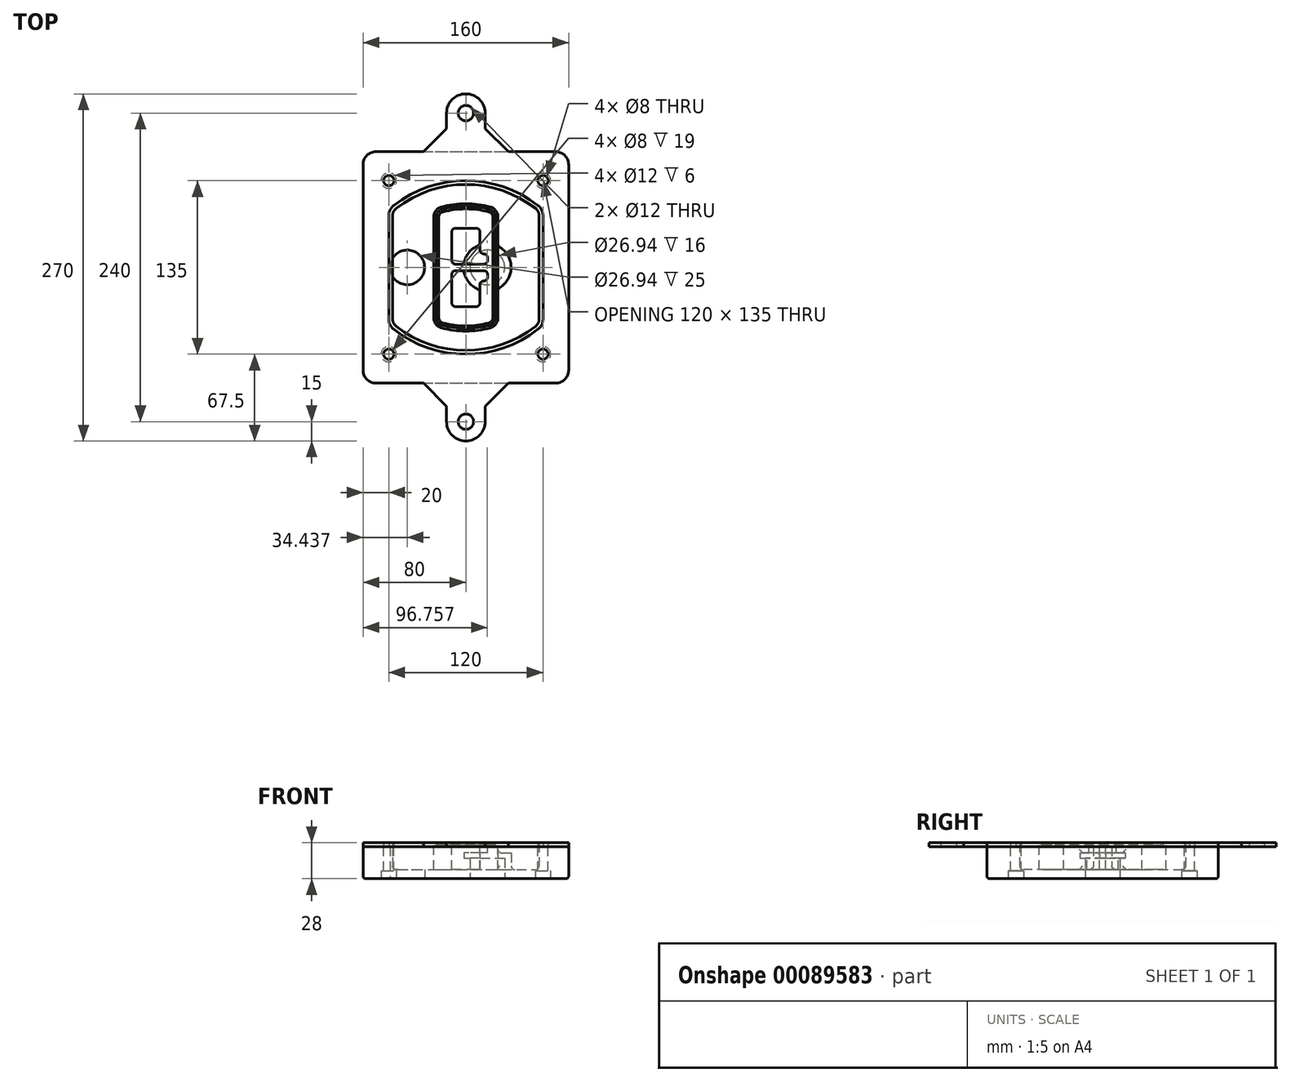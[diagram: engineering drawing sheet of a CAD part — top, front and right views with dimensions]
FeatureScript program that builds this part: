
annotation { "Feature Type Name" : "Feature", "Feature Type Description" : "" }
export const myFeature = defineFeature(function(context is Context, id is Id, definition is map)
    precondition{}
    {
        {
            var Q0;
            Q0=qCreatedBy(makeId("Top.planeOp"),FACE);
            var sketch = newSketch(context, id + "F0", { "sketchPlane" : qUnion([Q0])});
            skPoint(sketch, "E0.rect.middle", {"position": v(0, 0) * mm});
            skLineSegment(sketch, "E1.bottom", {"start": v(-70, -90) * mm, "end": v(70, -90) * mm});
            skLineSegment(sketch, "E1.top", {"start": v(-70, 90) * mm, "end": v(70, 90) * mm});
            skLineSegment(sketch, "E1.left", {"start": v(-80, -80) * mm, "end": v(-80, 80) * mm});
            skLineSegment(sketch, "E1.right", {"start": v(80, -80) * mm, "end": v(80, 80) * mm});
            skLineSegment(sketch, "E2", {"start": v(-80, 90) * mm, "end": v(80, -90) * mm, "construction": true});
            skLineSegment(sketch, "E3", {"start": v(80, 90) * mm, "end": v(-80, -90) * mm, "construction": true});
            skCircle(sketch, "E4", {"center": v(-60, 67.5) * mm, "radius": 4 * mm});
            skCircle(sketch, "E5", {"center": v(60, 67.5) * mm, "radius": 4 * mm});
            skCircle(sketch, "E6", {"center": v(60, -67.5) * mm, "radius": 4 * mm});
            skCircle(sketch, "E7", {"center": v(-60, -67.5) * mm, "radius": 4 * mm});
            skLineSegment(sketch, "E8", {"start": v(-60, 67.5) * mm, "end": v(60, 67.5) * mm, "construction": true});
            skLineSegment(sketch, "E9", {"start": v(60, 67.5) * mm, "end": v(60, -67.5) * mm, "construction": true});
            skLineSegment(sketch, "E10", {"start": v(60, -67.5) * mm, "end": v(-60, -67.5) * mm, "construction": true});
            skLineSegment(sketch, "E11", {"start": v(-60, -67.5) * mm, "end": v(-60, 67.5) * mm, "construction": true});
            skLineSegment(sketch, "E12", {"start": v(-60, 40.3) * mm, "end": v(-60, -40.3) * mm});
            skLineSegment(sketch, "E13", {"start": v(60, 40.3) * mm, "end": v(60, -40.3) * mm});
            skArc(sketch, "E14", {"start": v(56.15, 48.18) * mm, "mid": v(0, 67.5) * mm, "end": v(-56.15, 48.18) * mm});
            skArc(sketch, "E15", {"start": v(-56.15, -48.18) * mm, "mid": v(0, -67.5) * mm, "end": v(56.15, -48.18) * mm});
            skLineSegment(sketch, "E16", {"start": v(-60, 0) * mm, "end": v(60, 0) * mm, "construction": true});
            skPoint(sketch, "E17.visualSharp", {"position": v(-60, -45) * mm});
            skArc(sketch, "E17.filletArc", {"start": v(-60, -40.3) * mm, "mid": v(-58.99, -44.68) * mm, "end": v(-56.15, -48.18) * mm});
            skPoint(sketch, "E18.visualSharp", {"position": v(-60, 45) * mm});
            skArc(sketch, "E18.filletArc", {"start": v(-56.15, 48.18) * mm, "mid": v(-58.99, 44.68) * mm, "end": v(-60, 40.3) * mm});
            skPoint(sketch, "E19.visualSharp", {"position": v(60, 45) * mm});
            skArc(sketch, "E19.filletArc", {"start": v(60, 40.3) * mm, "mid": v(58.99, 44.68) * mm, "end": v(56.15, 48.18) * mm});
            skPoint(sketch, "E20.visualSharp", {"position": v(60, -45) * mm});
            skArc(sketch, "E20.filletArc", {"start": v(56.15, -48.18) * mm, "mid": v(58.99, -44.68) * mm, "end": v(60, -40.3) * mm});
            skPoint(sketch, "E21.visualSharp", {"position": v(-80, 90) * mm});
            skArc(sketch, "E21.filletArc", {"start": v(-70, 90) * mm, "mid": v(-77.07, 87.07) * mm, "end": v(-80, 80) * mm});
            skPoint(sketch, "E22.visualSharp", {"position": v(80, 90) * mm});
            skArc(sketch, "E22.filletArc", {"start": v(80, 80) * mm, "mid": v(77.07, 87.07) * mm, "end": v(70, 90) * mm});
            skPoint(sketch, "E23.visualSharp", {"position": v(80, -90) * mm});
            skArc(sketch, "E23.filletArc", {"start": v(70, -90) * mm, "mid": v(77.07, -87.07) * mm, "end": v(80, -80) * mm});
            skPoint(sketch, "E24.visualSharp", {"position": v(-80, -90) * mm});
            skArc(sketch, "E24.filletArc", {"start": v(-80, -80) * mm, "mid": v(-77.07, -87.07) * mm, "end": v(-70, -90) * mm});
            skArc(sketch, "E25.0", {"start": v(57, 40.3) * mm, "mid": v(56.3, 43.36) * mm, "end": v(54.3, 45.81) * mm});
            skLineSegment(sketch, "E25.1", {"start": v(57, 40.3) * mm, "end": v(57, -40.3) * mm});
            skArc(sketch, "E25.2", {"start": v(54.3, -45.81) * mm, "mid": v(56.3, -43.36) * mm, "end": v(57, -40.3) * mm});
            skArc(sketch, "E25.3", {"start": v(-54.3, -45.81) * mm, "mid": v(0, -64.5) * mm, "end": v(54.3, -45.81) * mm});
            skArc(sketch, "E25.4", {"start": v(-57, -40.3) * mm, "mid": v(-56.3, -43.36) * mm, "end": v(-54.3, -45.81) * mm});
            skArc(sketch, "E25.5", {"start": v(54.3, 45.81) * mm, "mid": v(0, 64.5) * mm, "end": v(-54.3, 45.81) * mm});
            skLineSegment(sketch, "E25.6", {"start": v(-57, 40.3) * mm, "end": v(-57, -40.3) * mm});
            skArc(sketch, "E25.7", {"start": v(-54.3, 45.81) * mm, "mid": v(-56.3, 43.36) * mm, "end": v(-57, 40.3) * mm});
            skArc(sketch, "E26.0", {"start": v(-58.62, 51.33) * mm, "mid": v(-62.58, 46.43) * mm, "end": v(-64, 40.3) * mm});
            skArc(sketch, "E26.1", {"start": v(58.62, 51.33) * mm, "mid": v(0, 71.5) * mm, "end": v(-58.62, 51.33) * mm});
            skArc(sketch, "E26.2", {"start": v(64, 40.3) * mm, "mid": v(62.58, 46.43) * mm, "end": v(58.62, 51.33) * mm});
            skLineSegment(sketch, "E26.3", {"start": v(64, 40.3) * mm, "end": v(64, -40.3) * mm});
            skArc(sketch, "E26.4", {"start": v(58.62, -51.33) * mm, "mid": v(62.58, -46.43) * mm, "end": v(64, -40.3) * mm});
            skLineSegment(sketch, "E26.5", {"start": v(-64, 40.3) * mm, "end": v(-64, -40.3) * mm});
            skArc(sketch, "E26.6", {"start": v(-58.62, -51.33) * mm, "mid": v(0, -71.5) * mm, "end": v(58.62, -51.33) * mm});
            skArc(sketch, "E26.7", {"start": v(-64, -40.3) * mm, "mid": v(-62.58, -46.43) * mm, "end": v(-58.62, -51.33) * mm});
            skSolve(sketch);
        }
        {
            var Q0;
            Q0=makeQuery(id+"F0.imprint","IMPRINT",FACE,{"disambiguationData":[TD([[makeQuery(id+"F0.imprint","IMPRINT",EDGE,{"derivedFrom":sQuery(id+"F0.wireOp",EDGE,"E1.bottom")}),1.0]])]});
            var Q1;
            Q1=makeQuery(id+"F0.imprint","IMPRINT",FACE,{"disambiguationData":[TD([[makeQuery(id+"F0.imprint","IMPRINT",EDGE,{"derivedFrom":sQuery(id+"F0.wireOp",EDGE,"E12")}),1.0]])]});
            var Q2;
            Q2=makeQuery(id+"F0.imprint","IMPRINT",FACE,{"disambiguationData":[TD([[makeQuery(id+"F0.imprint","IMPRINT",EDGE,{"derivedFrom":sQuery(id+"F0.wireOp",EDGE,"E25.0")}),1.0]])]});
            var Q3;
            Q3=makeQuery(id+"F0.imprint","IMPRINT",FACE,{"disambiguationData":[TD([[makeQuery(id+"F0.imprint","IMPRINT",EDGE,{"derivedFrom":sQuery(id+"F0.wireOp",EDGE,"E12")}),-1.0]])]});
            extrude(context, id + "F1", {"entities" : qUnion([Q0, Q1, Q2, Q3]), "oppositeDirection" : true, "depth" : 25 * mm});
        }
        {
            var Q0;
            Q0=makeQuery(id+"F0.imprint","IMPRINT",FACE,{"disambiguationData":[TD([[makeQuery(id+"F0.imprint","IMPRINT",EDGE,{"derivedFrom":sQuery(id+"F0.wireOp",EDGE,"E12")}),1.0]])]});
            extrude(context, id + "F2", {"entities" : qUnion([Q0]), "operationType" : NewBodyOperationType.ADD, "depth" : 3 * mm});
        }
        {
            var Q0;
            Q0=makeQuery(id+"F0.imprint","IMPRINT",FACE,{"disambiguationData":[TD([[makeQuery(id+"F0.imprint","IMPRINT",EDGE,{"derivedFrom":sQuery(id+"F0.wireOp",EDGE,"E25.0")}),1.0]])]});
            extrude(context, id + "F3", {"entities" : qUnion([Q0]), "operationType" : NewBodyOperationType.REMOVE, "oppositeDirection" : true, "depth" : 18 * mm});
        }
        {
            var Q0;
            Q0=makeQuery(id+"F2.opExtrude","CAP_FACE",FACE,{"disambiguationData":[OSD([sQuery(id+"F0.wireOp",EDGE,"E12"),sQuery(id+"F0.wireOp",EDGE,"E13"),sQuery(id+"F0.wireOp",EDGE,"E14"),sQuery(id+"F0.wireOp",EDGE,"E15"),sQuery(id+"F0.wireOp",EDGE,"E17.filletArc"),sQuery(id+"F0.wireOp",EDGE,"E18.filletArc"),sQuery(id+"F0.wireOp",EDGE,"E19.filletArc"),sQuery(id+"F0.wireOp",EDGE,"E20.filletArc"),sQuery(id+"F0.wireOp",EDGE,"E25.0"),sQuery(id+"F0.wireOp",EDGE,"E25.1"),sQuery(id+"F0.wireOp",EDGE,"E25.2"),sQuery(id+"F0.wireOp",EDGE,"E25.3"),sQuery(id+"F0.wireOp",EDGE,"E25.4"),sQuery(id+"F0.wireOp",EDGE,"E25.5"),sQuery(id+"F0.wireOp",EDGE,"E25.6"),sQuery(id+"F0.wireOp",EDGE,"E25.7")])],"isStart":false});
            var sketch = newSketch(context, id + "F4", { "sketchPlane" : qUnion([Q0])});
            skArc(sketch, "E27.0", {"start": v(-19.08, -46.97) * mm, "mid": v(0, -49.5) * mm, "end": v(19.08, -46.97) * mm});
            skArc(sketch, "E28.0", {"start": v(19.08, 46.97) * mm, "mid": v(0, 49.5) * mm, "end": v(-19.08, 46.97) * mm});
            skLineSegment(sketch, "E29", {"start": v(-25, 39.25) * mm, "end": v(-25, -39.25) * mm});
            skLineSegment(sketch, "E30", {"start": v(25, 39.25) * mm, "end": v(25, -39.25) * mm});
            skLineSegment(sketch, "E31", {"start": v(-25, 45.1) * mm, "end": v(25, 45.1) * mm, "construction": true});
            skLineSegment(sketch, "E32", {"start": v(-25, -45.1) * mm, "end": v(25, -45.1) * mm, "construction": true});
            skPoint(sketch, "E33.visualSharp", {"position": v(-25, 45.1) * mm});
            skArc(sketch, "E33.filletArc", {"start": v(-19.08, 46.97) * mm, "mid": v(-23.35, 44.11) * mm, "end": v(-25, 39.25) * mm});
            skPoint(sketch, "E34.visualSharp", {"position": v(25, 45.1) * mm});
            skArc(sketch, "E34.filletArc", {"start": v(25, 39.25) * mm, "mid": v(23.35, 44.11) * mm, "end": v(19.08, 46.97) * mm});
            skPoint(sketch, "E35.visualSharp", {"position": v(25, -45.1) * mm});
            skArc(sketch, "E35.filletArc", {"start": v(19.08, -46.97) * mm, "mid": v(23.35, -44.11) * mm, "end": v(25, -39.25) * mm});
            skPoint(sketch, "E36.visualSharp", {"position": v(-25, -45.1) * mm});
            skArc(sketch, "E36.filletArc", {"start": v(-25, -39.25) * mm, "mid": v(-23.35, -44.11) * mm, "end": v(-19.08, -46.97) * mm});
            skArc(sketch, "E37.0", {"start": v(54.3, 45.81) * mm, "mid": v(0, 64.5) * mm, "end": v(-54.3, 45.81) * mm});
            skArc(sketch, "E37.1", {"start": v(-54.3, 45.81) * mm, "mid": v(-56.3, 43.36) * mm, "end": v(-57, 40.3) * mm});
            skLineSegment(sketch, "E37.2", {"start": v(-57, 40.3) * mm, "end": v(-57, -40.3) * mm});
            skArc(sketch, "E37.3", {"start": v(-57, -40.3) * mm, "mid": v(-56.3, -43.36) * mm, "end": v(-54.3, -45.81) * mm});
            skArc(sketch, "E37.4", {"start": v(-54.3, -45.81) * mm, "mid": v(0, -64.5) * mm, "end": v(54.3, -45.81) * mm});
            skArc(sketch, "E37.5", {"start": v(54.3, -45.81) * mm, "mid": v(56.3, -43.36) * mm, "end": v(57, -40.3) * mm});
            skLineSegment(sketch, "E37.6", {"start": v(57, 40.3) * mm, "end": v(57, -40.3) * mm});
            skArc(sketch, "E37.7", {"start": v(57, 40.3) * mm, "mid": v(56.3, 43.36) * mm, "end": v(54.3, 45.81) * mm});
            skLineSegment(sketch, "E38.0", {"start": v(23, 39.25) * mm, "end": v(23, -39.25) * mm});
            skArc(sketch, "E38.1", {"start": v(18.56, -45.04) * mm, "mid": v(21.76, -42.9) * mm, "end": v(23, -39.25) * mm});
            skArc(sketch, "E38.2", {"start": v(-18.56, -45.04) * mm, "mid": v(0, -47.5) * mm, "end": v(18.56, -45.04) * mm});
            skArc(sketch, "E38.3", {"start": v(-23, -39.25) * mm, "mid": v(-21.76, -42.9) * mm, "end": v(-18.56, -45.04) * mm});
            skLineSegment(sketch, "E38.4", {"start": v(-23, 39.25) * mm, "end": v(-23, -39.25) * mm});
            skArc(sketch, "E38.5", {"start": v(23, 39.25) * mm, "mid": v(21.76, 42.9) * mm, "end": v(18.56, 45.04) * mm});
            skArc(sketch, "E38.6", {"start": v(-18.56, 45.04) * mm, "mid": v(-21.76, 42.9) * mm, "end": v(-23, 39.25) * mm});
            skArc(sketch, "E38.7", {"start": v(18.56, 45.04) * mm, "mid": v(0, 47.5) * mm, "end": v(-18.56, 45.04) * mm});
            skArc(sketch, "E39.0", {"start": v(21, 39.25) * mm, "mid": v(20.18, 41.68) * mm, "end": v(18.04, 43.1) * mm});
            skLineSegment(sketch, "E39.1", {"start": v(21, 39.25) * mm, "end": v(21, -39.25) * mm});
            skArc(sketch, "E39.2", {"start": v(18.04, -43.1) * mm, "mid": v(20.18, -41.68) * mm, "end": v(21, -39.25) * mm});
            skArc(sketch, "E39.3", {"start": v(-18.04, -43.1) * mm, "mid": v(0, -45.5) * mm, "end": v(18.04, -43.1) * mm});
            skArc(sketch, "E39.4", {"start": v(-21, -39.25) * mm, "mid": v(-20.18, -41.68) * mm, "end": v(-18.04, -43.1) * mm});
            skArc(sketch, "E39.5", {"start": v(18.04, 43.1) * mm, "mid": v(0, 45.5) * mm, "end": v(-18.04, 43.1) * mm});
            skLineSegment(sketch, "E39.6", {"start": v(-21, 39.25) * mm, "end": v(-21, -39.25) * mm});
            skArc(sketch, "E39.7", {"start": v(-18.04, 43.1) * mm, "mid": v(-20.18, 41.68) * mm, "end": v(-21, 39.25) * mm});
            skLineSegment(sketch, "E40", {"start": v(-25, 0) * mm, "end": v(25, 0) * mm, "construction": true});
            skLineSegment(sketch, "E41", {"start": v(-11, 5.5) * mm, "end": v(-11, 27.5) * mm});
            skLineSegment(sketch, "E42", {"start": v(-8, 30.5) * mm, "end": v(8, 30.5) * mm});
            skLineSegment(sketch, "E43", {"start": v(11, 27.5) * mm, "end": v(11, 13.5) * mm});
            skLineSegment(sketch, "E44", {"start": v(14, 10.5) * mm, "end": v(14, 10.5) * mm});
            skLineSegment(sketch, "E45", {"start": v(17, 7.5) * mm, "end": v(17, 5.5) * mm});
            skLineSegment(sketch, "E46", {"start": v(14, 2.5) * mm, "end": v(-8, 2.5) * mm});
            skPoint(sketch, "E47.visualSharp", {"position": v(-11, 30.5) * mm});
            skArc(sketch, "E47.filletArc", {"start": v(-8, 30.5) * mm, "mid": v(-10.12, 29.62) * mm, "end": v(-11, 27.5) * mm});
            skPoint(sketch, "E48.visualSharp", {"position": v(11, 30.5) * mm});
            skArc(sketch, "E48.filletArc", {"start": v(11, 27.5) * mm, "mid": v(10.12, 29.62) * mm, "end": v(8, 30.5) * mm});
            skPoint(sketch, "E49.visualSharp", {"position": v(11, 10.5) * mm});
            skArc(sketch, "E49.filletArc", {"start": v(11, 13.5) * mm, "mid": v(11.88, 11.38) * mm, "end": v(14, 10.5) * mm});
            skPoint(sketch, "E50.visualSharp", {"position": v(17, 10.5) * mm});
            skArc(sketch, "E50.filletArc", {"start": v(17, 7.5) * mm, "mid": v(16.12, 9.62) * mm, "end": v(14, 10.5) * mm});
            skPoint(sketch, "E51.visualSharp", {"position": v(17, 2.5) * mm});
            skArc(sketch, "E51.filletArc", {"start": v(14, 2.5) * mm, "mid": v(16.12, 3.38) * mm, "end": v(17, 5.5) * mm});
            skPoint(sketch, "E52.visualSharp", {"position": v(-11, 2.5) * mm});
            skArc(sketch, "E52.filletArc", {"start": v(-11, 5.5) * mm, "mid": v(-10.12, 3.38) * mm, "end": v(-8, 2.5) * mm});
            skLineSegment(sketch, "E53.0.MirrorCS", {"start": v(14, -2.5) * mm, "end": v(-8, -2.5) * mm});
            skArc(sketch, "E54.0.MirrorCS", {"start": v(-11, -5.5) * mm, "mid": v(-10.12, -3.38) * mm, "end": v(-8, -2.5) * mm});
            skLineSegment(sketch, "E55.0.MirrorCS", {"start": v(-11, -5.5) * mm, "end": v(-11, -27.5) * mm});
            skArc(sketch, "E56.0.MirrorCS", {"start": v(-8, -30.5) * mm, "mid": v(-10.12, -29.62) * mm, "end": v(-11, -27.5) * mm});
            skLineSegment(sketch, "E57.0.MirrorCS", {"start": v(-8, -30.5) * mm, "end": v(8, -30.5) * mm});
            skArc(sketch, "E58.0.MirrorCS", {"start": v(11, -27.5) * mm, "mid": v(10.12, -29.62) * mm, "end": v(8, -30.5) * mm});
            skLineSegment(sketch, "E59.0.MirrorCS", {"start": v(11, -27.5) * mm, "end": v(11, -13.5) * mm});
            skArc(sketch, "E60.0.MirrorCS", {"start": v(11, -13.5) * mm, "mid": v(11.88, -11.38) * mm, "end": v(14, -10.5) * mm});
            skArc(sketch, "E61.0.MirrorCS", {"start": v(17, -7.5) * mm, "mid": v(16.12, -9.62) * mm, "end": v(14, -10.5) * mm});
            skLineSegment(sketch, "E62.0.MirrorCS", {"start": v(17, -7.5) * mm, "end": v(17, -5.5) * mm});
            skArc(sketch, "E63.0.MirrorCS", {"start": v(14, -2.5) * mm, "mid": v(16.12, -3.38) * mm, "end": v(17, -5.5) * mm});
            skSolve(sketch);
        }
        {
            var Q0;
            Q0=makeQuery(id+"F4.imprint","IMPRINT",FACE,{"disambiguationData":[TD([[makeQuery(id+"F4.imprint","IMPRINT",EDGE,{"derivedFrom":sQuery(id+"F4.wireOp",EDGE,"E27.0")}),1.0]])]});
            var Q1;
            Q1=makeQuery(id+"F4.imprint","IMPRINT",FACE,{"disambiguationData":[TD([[makeQuery(id+"F4.imprint","IMPRINT",EDGE,{"derivedFrom":sQuery(id+"F4.wireOp",EDGE,"E38.0")}),-1.0]])]});
            var Q2;
            Q2=makeQuery(id+"F4.imprint","IMPRINT",FACE,{"disambiguationData":[TD([[makeQuery(id+"F4.imprint","IMPRINT",EDGE,{"derivedFrom":sQuery(id+"F4.wireOp",EDGE,"E39.0")}),1.0]])]});
            extrude(context, id + "F5", {"entities" : qUnion([Q0, Q1, Q2]), "operationType" : NewBodyOperationType.ADD, "endBound" : BoundingType.UP_TO_NEXT, "oppositeDirection" : true, "depth" : 25 * mm});
        }
        {
            var Q0;
            Q0=makeQuery(id+"F4.imprint","IMPRINT",FACE,{"disambiguationData":[TD([[makeQuery(id+"F4.imprint","IMPRINT",EDGE,{"derivedFrom":sQuery(id+"F4.wireOp",EDGE,"E38.0")}),-1.0]])]});
            extrude(context, id + "F6", {"entities" : qUnion([Q0]), "operationType" : NewBodyOperationType.REMOVE, "oppositeDirection" : true, "depth" : 2 * mm});
        }
        {
            var Q0;
            Q0=makeQuery(id+"F1.opExtrude","CAP_FACE",FACE,{"disambiguationData":[OSD([sQuery(id+"F0.wireOp",EDGE,"E1.bottom"),sQuery(id+"F0.wireOp",EDGE,"E1.top"),sQuery(id+"F0.wireOp",EDGE,"E1.left"),sQuery(id+"F0.wireOp",EDGE,"E1.right"),sQuery(id+"F0.wireOp",EDGE,"E4"),sQuery(id+"F0.wireOp",EDGE,"E5"),sQuery(id+"F0.wireOp",EDGE,"E6"),sQuery(id+"F0.wireOp",EDGE,"E7"),sQuery(id+"F0.wireOp",EDGE,"E21.filletArc"),sQuery(id+"F0.wireOp",EDGE,"E22.filletArc"),sQuery(id+"F0.wireOp",EDGE,"E23.filletArc"),sQuery(id+"F0.wireOp",EDGE,"E24.filletArc")])],"isStart":false});
            var sketch = newSketch(context, id + "F7", { "sketchPlane" : qUnion([Q0])});
            skCircle(sketch, "E64", {"center": v(16.76, 0) * mm, "radius": 13.47 * mm});
            skCircle(sketch, "E65", {"center": v(-45.56, 0) * mm, "radius": 13.47 * mm});
            skLineSegment(sketch, "E66", {"start": v(80, 0) * mm, "end": v(-80, 0) * mm});
            skCircle(sketch, "E67", {"center": v(16.76, 0) * mm, "radius": 18.47 * mm});
            skCircle(sketch, "E68", {"center": v(60, -67.5) * mm, "radius": 6 * mm});
            skCircle(sketch, "E69", {"center": v(-60, -67.5) * mm, "radius": 6 * mm});
            skCircle(sketch, "E70", {"center": v(-60, 67.5) * mm, "radius": 6 * mm});
            skCircle(sketch, "E71", {"center": v(60, 67.5) * mm, "radius": 6 * mm});
            skSolve(sketch);
        }
        {
            var Q0;
            {var subQ1=sQuery(id+"F7.wireOp",EDGE,"E66");var subQ4=sQuery(id+"F7.wireOp",EDGE,"E64");var subQ6=makeQuery(id+"F7.imprint","INTERSECT",VERTEX,{"disambiguationData":[OD(0.0)],"derivedFrom":[subQ4,subQ1]});Q0=makeQuery(id+"F7.imprint","IMPRINT",FACE,{"disambiguationData":[TD([[makeQuery(id+"F7.imprint","IMPRINT",EDGE,{"disambiguationData":[TD([[subQ6,-1.0]])],"derivedFrom":subQ4}),-1.0]])]});}
            var Q1;
            {var subQ0=sQuery(id+"F7.wireOp",EDGE,"E66");var subQ1=sQuery(id+"F7.wireOp",EDGE,"E64");var subQ3=makeQuery(id+"F7.imprint","INTERSECT",VERTEX,{"disambiguationData":[OD(0.0)],"derivedFrom":[subQ1,subQ0]});Q1=makeQuery(id+"F7.imprint","IMPRINT",FACE,{"disambiguationData":[TD([[makeQuery(id+"F7.imprint","IMPRINT",EDGE,{"disambiguationData":[TD([[subQ3,-1.0]])],"derivedFrom":subQ1}),1.0]])]});}
            var Q2;
            {var subQ0=sQuery(id+"F7.wireOp",EDGE,"E66");var subQ1=sQuery(id+"F7.wireOp",EDGE,"E64");var subQ3=makeQuery(id+"F7.imprint","INTERSECT",VERTEX,{"disambiguationData":[OD(0.0)],"derivedFrom":[subQ1,subQ0]});Q2=makeQuery(id+"F7.imprint","IMPRINT",FACE,{"disambiguationData":[TD([[makeQuery(id+"F7.imprint","IMPRINT",EDGE,{"disambiguationData":[TD([[subQ3,1.0]])],"derivedFrom":subQ1}),1.0]])]});}
            var Q3;
            {var subQ1=sQuery(id+"F7.wireOp",EDGE,"E66");var subQ4=sQuery(id+"F7.wireOp",EDGE,"E64");var subQ6=makeQuery(id+"F7.imprint","INTERSECT",VERTEX,{"disambiguationData":[OD(0.0)],"derivedFrom":[subQ4,subQ1]});Q3=makeQuery(id+"F7.imprint","IMPRINT",FACE,{"disambiguationData":[TD([[makeQuery(id+"F7.imprint","IMPRINT",EDGE,{"disambiguationData":[TD([[subQ6,1.0]])],"derivedFrom":subQ4}),-1.0]])]});}
            extrude(context, id + "F8", {"entities" : qUnion([Q0, Q1, Q2, Q3]), "operationType" : NewBodyOperationType.ADD, "oppositeDirection" : true, "depth" : 20 * mm});
        }
        {
            var Q0;
            {var subQ0=sQuery(id+"F7.wireOp",EDGE,"E66");var subQ1=sQuery(id+"F7.wireOp",EDGE,"E64");var subQ3=makeQuery(id+"F7.imprint","INTERSECT",VERTEX,{"disambiguationData":[OD(0.0)],"derivedFrom":[subQ1,subQ0]});Q0=makeQuery(id+"F7.imprint","IMPRINT",FACE,{"disambiguationData":[TD([[makeQuery(id+"F7.imprint","IMPRINT",EDGE,{"disambiguationData":[TD([[subQ3,-1.0]])],"derivedFrom":subQ1}),1.0]])]});}
            var Q1;
            {var subQ0=sQuery(id+"F7.wireOp",EDGE,"E66");var subQ1=sQuery(id+"F7.wireOp",EDGE,"E64");var subQ3=makeQuery(id+"F7.imprint","INTERSECT",VERTEX,{"disambiguationData":[OD(0.0)],"derivedFrom":[subQ1,subQ0]});Q1=makeQuery(id+"F7.imprint","IMPRINT",FACE,{"disambiguationData":[TD([[makeQuery(id+"F7.imprint","IMPRINT",EDGE,{"disambiguationData":[TD([[subQ3,1.0]])],"derivedFrom":subQ1}),1.0]])]});}
            extrude(context, id + "F9", {"entities" : qUnion([Q0, Q1]), "operationType" : NewBodyOperationType.REMOVE, "oppositeDirection" : true, "depth" : 16 * mm});
        }
        {
            var Q0;
            {var subQ0=sQuery(id+"F7.wireOp",EDGE,"E66");var subQ1=sQuery(id+"F7.wireOp",EDGE,"E65");var subQ3=makeQuery(id+"F7.imprint","INTERSECT",VERTEX,{"disambiguationData":[OD(0.0)],"derivedFrom":[subQ1,subQ0]});Q0=makeQuery(id+"F7.imprint","IMPRINT",FACE,{"disambiguationData":[TD([[makeQuery(id+"F7.imprint","IMPRINT",EDGE,{"disambiguationData":[TD([[subQ3,-1.0]])],"derivedFrom":subQ1}),1.0]])]});}
            var Q1;
            {var subQ0=sQuery(id+"F7.wireOp",EDGE,"E66");var subQ1=sQuery(id+"F7.wireOp",EDGE,"E65");var subQ3=makeQuery(id+"F7.imprint","INTERSECT",VERTEX,{"disambiguationData":[OD(0.0)],"derivedFrom":[subQ1,subQ0]});Q1=makeQuery(id+"F7.imprint","IMPRINT",FACE,{"disambiguationData":[TD([[makeQuery(id+"F7.imprint","IMPRINT",EDGE,{"disambiguationData":[TD([[subQ3,1.0]])],"derivedFrom":subQ1}),1.0]])]});}
            extrude(context, id + "F10", {"entities" : qUnion([Q0, Q1]), "operationType" : NewBodyOperationType.REMOVE, "oppositeDirection" : true, "depth" : 25 * mm});
        }
        {
            var Q0;
            Q0=makeQuery(id+"F7.imprint","IMPRINT",FACE,{"disambiguationData":[TD([[makeQuery(id+"F7.imprint","IMPRINT",EDGE,{"derivedFrom":sQuery(id+"F7.wireOp",EDGE,"E68")}),1.0]])]});
            var Q1;
            Q1=makeQuery(id+"F7.imprint","IMPRINT",FACE,{"disambiguationData":[TD([[makeQuery(id+"F7.imprint","IMPRINT",EDGE,{"derivedFrom":makeQuery(id+"F1.opExtrude","CAP_EDGE",EDGE,{"disambiguationData":[OSD([sQuery(id+"F0.wireOp",EDGE,"E5")])],"isStart":false})}),-1.0]])]});
            var Q2;
            Q2=makeQuery(id+"F7.imprint","IMPRINT",FACE,{"disambiguationData":[TD([[makeQuery(id+"F7.imprint","IMPRINT",EDGE,{"derivedFrom":sQuery(id+"F7.wireOp",EDGE,"E69")}),1.0]])]});
            var Q3;
            Q3=makeQuery(id+"F7.imprint","IMPRINT",FACE,{"disambiguationData":[TD([[makeQuery(id+"F7.imprint","IMPRINT",EDGE,{"derivedFrom":makeQuery(id+"F1.opExtrude","CAP_EDGE",EDGE,{"disambiguationData":[OSD([sQuery(id+"F0.wireOp",EDGE,"E4")])],"isStart":false})}),-1.0]])]});
            var Q4;
            Q4=makeQuery(id+"F7.imprint","IMPRINT",FACE,{"disambiguationData":[TD([[makeQuery(id+"F7.imprint","IMPRINT",EDGE,{"derivedFrom":sQuery(id+"F7.wireOp",EDGE,"E70")}),1.0]])]});
            var Q5;
            Q5=makeQuery(id+"F7.imprint","IMPRINT",FACE,{"disambiguationData":[TD([[makeQuery(id+"F7.imprint","IMPRINT",EDGE,{"derivedFrom":makeQuery(id+"F1.opExtrude","CAP_EDGE",EDGE,{"disambiguationData":[OSD([sQuery(id+"F0.wireOp",EDGE,"E7")])],"isStart":false})}),-1.0]])]});
            var Q6;
            Q6=makeQuery(id+"F7.imprint","IMPRINT",FACE,{"disambiguationData":[TD([[makeQuery(id+"F7.imprint","IMPRINT",EDGE,{"derivedFrom":sQuery(id+"F7.wireOp",EDGE,"E71")}),1.0]])]});
            var Q7;
            Q7=makeQuery(id+"F7.imprint","IMPRINT",FACE,{"disambiguationData":[TD([[makeQuery(id+"F7.imprint","IMPRINT",EDGE,{"derivedFrom":makeQuery(id+"F1.opExtrude","CAP_EDGE",EDGE,{"disambiguationData":[OSD([sQuery(id+"F0.wireOp",EDGE,"E6")])],"isStart":false})}),-1.0]])]});
            extrude(context, id + "F11", {"entities" : qUnion([Q0, Q1, Q2, Q3, Q4, Q5, Q6, Q7]), "operationType" : NewBodyOperationType.REMOVE, "oppositeDirection" : true, "depth" : 6 * mm});
        }
        {
            var Q0;
            Q0=makeQuery(id+"F9.boolean.opBoolean","COPY",FACE,{"derivedFrom":makeQuery(id+"F9.opExtrude","CAP_FACE",FACE,{"disambiguationData":[OSD([sQuery(id+"F7.wireOp",EDGE,"E64")])],"isStart":false})});
            var sketch = newSketch(context, id + "F12", { "sketchPlane" : qUnion([Q0])});
            skArc(sketch, "E72.0", {"start": v(11, 17.55) * mm, "mid": v(2.57, 11.82) * mm, "end": v(-1.54, 2.5) * mm});
            skArc(sketch, "E72.1", {"start": v(-1.54, -2.5) * mm, "mid": v(2.57, -11.82) * mm, "end": v(11, -17.55) * mm});
            skLineSegment(sketch, "E73", {"start": v(-1.54, -2.5) * mm, "end": v(14, -2.5) * mm});
            skLineSegment(sketch, "E74.0", {"start": v(14, 2.5) * mm, "end": v(-1.54, 2.5) * mm});
            skArc(sketch, "E74.1", {"start": v(14, 2.5) * mm, "mid": v(16.12, 3.38) * mm, "end": v(17, 5.5) * mm});
            skLineSegment(sketch, "E74.2", {"start": v(17, 7.5) * mm, "end": v(17, 5.5) * mm});
            skArc(sketch, "E74.3", {"start": v(17, 7.5) * mm, "mid": v(16.12, 9.62) * mm, "end": v(14, 10.5) * mm});
            skArc(sketch, "E74.4", {"start": v(11, 13.5) * mm, "mid": v(11.88, 11.38) * mm, "end": v(14, 10.5) * mm});
            skLineSegment(sketch, "E74.5", {"start": v(11, 17.55) * mm, "end": v(11, 13.5) * mm});
            skLineSegment(sketch, "E74.7", {"start": v(14, -2.5) * mm, "end": v(-1.54, -2.5) * mm});
            skArc(sketch, "E74.8", {"start": v(14, -2.5) * mm, "mid": v(16.12, -3.38) * mm, "end": v(17, -5.5) * mm});
            skLineSegment(sketch, "E74.9", {"start": v(17, -7.5) * mm, "end": v(17, -5.5) * mm});
            skArc(sketch, "E74.10", {"start": v(17, -7.5) * mm, "mid": v(16.12, -9.62) * mm, "end": v(14, -10.5) * mm});
            skArc(sketch, "E74.11", {"start": v(11, -13.5) * mm, "mid": v(11.88, -11.38) * mm, "end": v(14, -10.5) * mm});
            skLineSegment(sketch, "E74.12", {"start": v(11, -17.55) * mm, "end": v(11, -13.5) * mm});
            skPoint(sketch, "E75.orphan", {"position": v(11, -27.5) * mm});
            skPoint(sketch, "E76.orphan", {"position": v(-8, -2.5) * mm});
            skPoint(sketch, "E77.orphan", {"position": v(-8, 2.5) * mm});
            skPoint(sketch, "E78.orphan", {"position": v(11, 27.5) * mm});
            skSolve(sketch);
        }
        {
            var Q0;
            {var subQ7=sQuery(id+"F12.wireOp",EDGE,"E72.0");var subQ14=sQuery(id+"F12.wireOp",EDGE,"E72.1");var subQ16=sQuery(id+"F12.wireOp",EDGE,"E74.1");var subQ18=sQuery(id+"F12.wireOp",EDGE,"E74.8");Q0=qUnion([makeQuery(id+"F12.imprint","IMPRINT",FACE,{"disambiguationData":[TD([[makeQuery(id+"F12.imprint","IMPRINT",EDGE,{"derivedFrom":subQ7}),1.0]])]}),makeQuery(id+"F12.imprint","IMPRINT",FACE,{"disambiguationData":[TD([[makeQuery(id+"F12.imprint","IMPRINT",EDGE,{"derivedFrom":subQ14}),1.0]])]}),makeQuery(id+"F12.imprint","IMPRINT",FACE,{"disambiguationData":[TD([[makeQuery(id+"F12.imprint","IMPRINT",EDGE,{"derivedFrom":subQ16}),1.0]])]}),makeQuery(id+"F12.imprint","IMPRINT",FACE,{"disambiguationData":[TD([[makeQuery(id+"F12.imprint","IMPRINT",EDGE,{"derivedFrom":subQ18}),-1.0]])]})]);}
            var Q1;
            Q1=makeQuery(id+"F5.boolean.opBoolean","SPLIT",FACE,{"disambiguationData":[TD([makeQuery(id+"F5.opExtrude","SWEPT_FACE",FACE,{"disambiguationData":[OSD([sQuery(id+"F4.wireOp",EDGE,"E41")])]})])],"derivedFrom":makeQuery(id+"F3.boolean.opBoolean","COPY",FACE,{"derivedFrom":makeQuery(id+"F3.opExtrude","CAP_FACE",FACE,{"disambiguationData":[OSD([sQuery(id+"F0.wireOp",EDGE,"E25.0"),sQuery(id+"F0.wireOp",EDGE,"E25.1"),sQuery(id+"F0.wireOp",EDGE,"E25.2"),sQuery(id+"F0.wireOp",EDGE,"E25.3"),sQuery(id+"F0.wireOp",EDGE,"E25.4"),sQuery(id+"F0.wireOp",EDGE,"E25.5"),sQuery(id+"F0.wireOp",EDGE,"E25.6"),sQuery(id+"F0.wireOp",EDGE,"E25.7")])],"isStart":false})})});
            extrude(context, id + "F13", {"entities" : qUnion([Q0]), "operationType" : NewBodyOperationType.REMOVE, "endBound" : BoundingType.UP_TO_SURFACE, "endBoundEntityFace" : qUnion([Q1]), "depth" : 25 * mm});
        }
        {
            var Q0;
            Q0=makeQuery(id+"F3.boolean.opBoolean","COPY",EDGE,{"derivedFrom":makeQuery(id+"F3.opExtrude","CAP_EDGE",EDGE,{"disambiguationData":[OSD([sQuery(id+"F0.wireOp",EDGE,"E25.6")])],"isStart":false})});
            var Q1;
            Q1=makeQuery(id+"F8.boolean.opBoolean","INTERSECT",EDGE,{"derivedFrom":[makeQuery(id+"F5.opExtrude","SWEPT_FACE",FACE,{"disambiguationData":[OSD([sQuery(id+"F4.wireOp",EDGE,"E30")])]}),makeQuery(id+"F8.opExtrude","CAP_FACE",FACE,{"disambiguationData":[OSD([sQuery(id+"F7.wireOp",EDGE,"E67")])],"isStart":false})]});
            var Q2;
            Q2=makeQuery(id+"F8.boolean.opBoolean","INTERSECT",EDGE,{"disambiguationData":[OD(1.0)],"derivedFrom":[makeQuery(id+"F5.opExtrude","SWEPT_FACE",FACE,{"disambiguationData":[OSD([sQuery(id+"F4.wireOp",EDGE,"E30")])]}),makeQuery(id+"F8.opExtrude","SWEPT_FACE",FACE,{"disambiguationData":[OSD([sQuery(id+"F7.wireOp",EDGE,"E67")])]})]});
            var Q3;
            {var subQ0=makeQuery(id+"F3.boolean.opBoolean","COPY",FACE,{"derivedFrom":makeQuery(id+"F3.opExtrude","CAP_FACE",FACE,{"disambiguationData":[OSD([sQuery(id+"F0.wireOp",EDGE,"E25.0"),sQuery(id+"F0.wireOp",EDGE,"E25.1"),sQuery(id+"F0.wireOp",EDGE,"E25.2"),sQuery(id+"F0.wireOp",EDGE,"E25.3"),sQuery(id+"F0.wireOp",EDGE,"E25.4"),sQuery(id+"F0.wireOp",EDGE,"E25.5"),sQuery(id+"F0.wireOp",EDGE,"E25.6"),sQuery(id+"F0.wireOp",EDGE,"E25.7")])],"isStart":false})});var subQ1=sQuery(id+"F4.wireOp",EDGE,"E30");Q3=makeQuery(id+"F8.boolean.opBoolean","SPLIT",EDGE,{"disambiguationData":[TD([makeQuery(id+"F5.opExtrude","SWEPT_FACE",FACE,{"disambiguationData":[OSD([sQuery(id+"F4.wireOp",EDGE,"E35.filletArc")])]})])],"derivedFrom":makeQuery(id+"F5.opExtrude","TWEAK_EDGE",EDGE,{"derivedFrom":[subQ0,makeQuery(id+"F4.imprint","IMPRINT",EDGE,{"derivedFrom":subQ1})]})});}
            var Q4;
            {var subQ0=sQuery(id+"F0.wireOp",EDGE,"E25.0");var subQ1=sQuery(id+"F0.wireOp",EDGE,"E25.1");var subQ2=sQuery(id+"F0.wireOp",EDGE,"E25.2");var subQ3=sQuery(id+"F0.wireOp",EDGE,"E25.3");var subQ4=sQuery(id+"F0.wireOp",EDGE,"E25.4");var subQ5=sQuery(id+"F0.wireOp",EDGE,"E25.5");var subQ6=sQuery(id+"F0.wireOp",EDGE,"E25.6");var subQ7=sQuery(id+"F0.wireOp",EDGE,"E25.7");Q4=makeQuery(id+"F8.boolean.opBoolean","INTERSECT",EDGE,{"derivedFrom":[makeQuery(id+"F5.boolean.opBoolean","SPLIT",FACE,{"disambiguationData":[TD([makeQuery(id+"F2.opExtrude","SWEPT_FACE",FACE,{"disambiguationData":[OSD([subQ0])]})])],"derivedFrom":makeQuery(id+"F3.boolean.opBoolean","COPY",FACE,{"derivedFrom":makeQuery(id+"F3.opExtrude","CAP_FACE",FACE,{"disambiguationData":[OSD([subQ0,subQ1,subQ2,subQ3,subQ4,subQ5,subQ6,subQ7])],"isStart":false})})}),makeQuery(id+"F8.opExtrude","SWEPT_FACE",FACE,{"disambiguationData":[OSD([sQuery(id+"F7.wireOp",EDGE,"E67")])]})]});}
            var Q5;
            Q5=makeQuery(id+"F8.boolean.opBoolean","INTERSECT",EDGE,{"disambiguationData":[OD(0.0)],"derivedFrom":[makeQuery(id+"F5.opExtrude","SWEPT_FACE",FACE,{"disambiguationData":[OSD([sQuery(id+"F4.wireOp",EDGE,"E30")])]}),makeQuery(id+"F8.opExtrude","SWEPT_FACE",FACE,{"disambiguationData":[OSD([sQuery(id+"F7.wireOp",EDGE,"E67")])]})]});
            fillet(context, id + "F14", {"entities" : qUnion([Q0, Q1, Q2, Q3, Q4, Q5]), "radius" : 3 * mm, "tangentPropagation" : true, "allowEdgeOverflow" : false});
        }
        {
            var Q0;
            Q0=makeQuery(id+"F1.opExtrude","CAP_EDGE",EDGE,{"disambiguationData":[OSD([sQuery(id+"F0.wireOp",EDGE,"E1.bottom")])],"isStart":false});
            fillet(context, id + "F15", {"entities" : qUnion([Q0]), "radius" : 2 * mm, "tangentPropagation" : true, "allowEdgeOverflow" : false});
        }
        {
            var Q0;
            {var subQ0=sQuery(id+"F0.wireOp",EDGE,"E22.filletArc");var subQ1=sQuery(id+"F0.wireOp",EDGE,"E7");var subQ2=sQuery(id+"F0.wireOp",EDGE,"E6");var subQ3=sQuery(id+"F0.wireOp",EDGE,"E5");var subQ4=sQuery(id+"F0.wireOp",EDGE,"E4");var subQ5=sQuery(id+"F0.wireOp",EDGE,"E1.bottom");var subQ6=sQuery(id+"F0.wireOp",EDGE,"E21.filletArc");var subQ7=sQuery(id+"F0.wireOp",EDGE,"E1.top");var subQ8=sQuery(id+"F0.wireOp",EDGE,"E1.left");var subQ9=sQuery(id+"F0.wireOp",EDGE,"E1.right");var subQ10=sQuery(id+"F0.wireOp",EDGE,"E23.filletArc");var subQ11=sQuery(id+"F0.wireOp",EDGE,"E24.filletArc");Q0=makeQuery(id+"F2.boolean.opBoolean","SPLIT",FACE,{"disambiguationData":[TD([makeQuery(id+"F1.opExtrude","SWEPT_FACE",FACE,{"disambiguationData":[OSD([subQ5])]})])],"derivedFrom":makeQuery(id+"F1.opExtrude","CAP_FACE",FACE,{"disambiguationData":[OSD([subQ5,subQ7,subQ8,subQ9,subQ4,subQ3,subQ2,subQ1,subQ6,subQ0,subQ10,subQ11])],"isStart":true})});}
            var sketch = newSketch(context, id + "F16", { "sketchPlane" : qUnion([Q0])});
            skLineSegment(sketch, "E79", {"start": v(0, 90) * mm, "end": v(0, 120) * mm, "construction": true});
            skCircle(sketch, "E80", {"center": v(0, 120) * mm, "radius": 6 * mm});
            skArc(sketch, "E81", {"start": v(15, 120) * mm, "mid": v(0, 135) * mm, "end": v(-15, 120) * mm});
            skLineSegment(sketch, "E82", {"start": v(-15, 120) * mm, "end": v(-15, 108) * mm});
            skLineSegment(sketch, "E83", {"start": v(-15, 108) * mm, "end": v(-33, 90) * mm});
            skLineSegment(sketch, "E84.MirrorCS", {"start": v(15, 120) * mm, "end": v(15, 108) * mm});
            skLineSegment(sketch, "E85.MirrorCS", {"start": v(15, 108) * mm, "end": v(33, 90) * mm});
            skLineSegment(sketch, "E86", {"start": v(-80, 0) * mm, "end": v(80, 0) * mm, "construction": true});
            skLineSegment(sketch, "E87.MirrorCS", {"start": v(15, -108) * mm, "end": v(33, -90) * mm});
            skLineSegment(sketch, "E88.MirrorCS", {"start": v(15, -120) * mm, "end": v(15, -108) * mm});
            skArc(sketch, "E89.MirrorCS", {"start": v(15, -120) * mm, "mid": v(0, -135) * mm, "end": v(-15, -120) * mm});
            skCircle(sketch, "E90.MirrorC", {"center": v(0, -120) * mm, "radius": 6 * mm});
            skLineSegment(sketch, "E91.MirrorCS", {"start": v(-15, -120) * mm, "end": v(-15, -108) * mm});
            skLineSegment(sketch, "E92.MirrorCS", {"start": v(-15, -108) * mm, "end": v(-33, -90) * mm});
            skLineSegment(sketch, "E93.MirrorCS", {"start": v(0, -90) * mm, "end": v(0, -120) * mm, "construction": true});
            skSolve(sketch);
        }
        {
            var Q0;
            Q0=makeQuery(id+"F16.imprint","IMPRINT",FACE,{"disambiguationData":[TD([[makeQuery(id+"F16.imprint","IMPRINT",EDGE,{"derivedFrom":sQuery(id+"F16.wireOp",EDGE,"E80")}),-1.0]])]});
            var Q1;
            {var subQ0=sQuery(id+"F16.wireOp",EDGE,"E87.MirrorCS");Q1=makeQuery(id+"F16.imprint","IMPRINT",FACE,{"disambiguationData":[TD([[makeQuery(id+"F16.imprint","IMPRINT",EDGE,{"derivedFrom":subQ0}),1.0]])]});}
            var Q2;
            Q2=makeQuery(id+"F16.imprint","IMPRINT",FACE,{"disambiguationData":[TD([[makeQuery(id+"F16.imprint","IMPRINT",EDGE,{"derivedFrom":makeQuery(id+"F1.opExtrude","CAP_EDGE",EDGE,{"disambiguationData":[OSD([sQuery(id+"F0.wireOp",EDGE,"E1.left")])],"isStart":true})}),-1.0]])]});
            var Q3;
            Q3=makeQuery(id+"F2.opExtrude","CAP_FACE",FACE,{"disambiguationData":[OSD([sQuery(id+"F0.wireOp",EDGE,"E12"),sQuery(id+"F0.wireOp",EDGE,"E13"),sQuery(id+"F0.wireOp",EDGE,"E14"),sQuery(id+"F0.wireOp",EDGE,"E15"),sQuery(id+"F0.wireOp",EDGE,"E17.filletArc"),sQuery(id+"F0.wireOp",EDGE,"E18.filletArc"),sQuery(id+"F0.wireOp",EDGE,"E19.filletArc"),sQuery(id+"F0.wireOp",EDGE,"E20.filletArc"),sQuery(id+"F0.wireOp",EDGE,"E25.0"),sQuery(id+"F0.wireOp",EDGE,"E25.1"),sQuery(id+"F0.wireOp",EDGE,"E25.2"),sQuery(id+"F0.wireOp",EDGE,"E25.3"),sQuery(id+"F0.wireOp",EDGE,"E25.4"),sQuery(id+"F0.wireOp",EDGE,"E25.5"),sQuery(id+"F0.wireOp",EDGE,"E25.6"),sQuery(id+"F0.wireOp",EDGE,"E25.7")])],"isStart":false});
            extrude(context, id + "F17", {"entities" : qUnion([Q0, Q1, Q2]), "endBound" : BoundingType.UP_TO_SURFACE, "endBoundEntityFace" : qUnion([Q3]), "depth" : 25 * mm});
        }
    });
